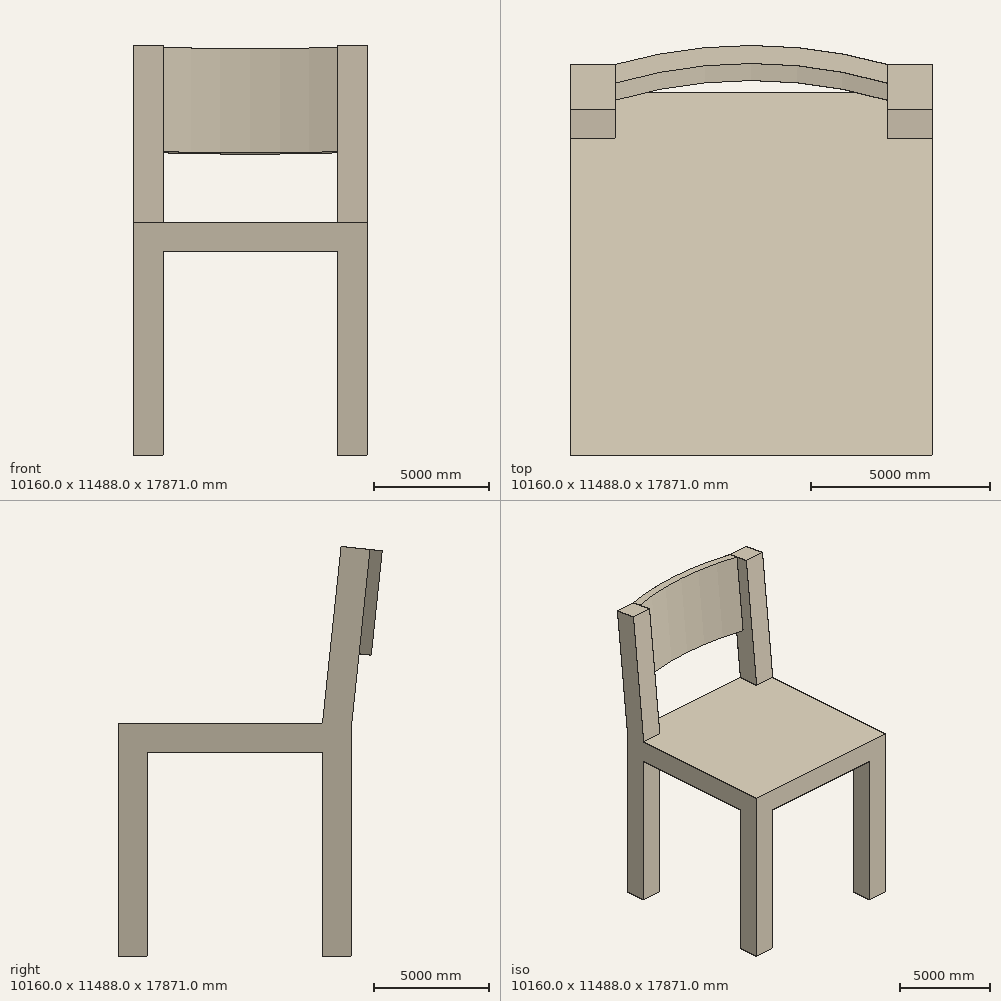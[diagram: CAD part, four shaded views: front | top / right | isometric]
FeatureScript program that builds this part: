
annotation { "Feature Type Name" : "Feature", "Feature Type Description" : "" }
export const myFeature = defineFeature(function(context is Context, id is Id, definition is map)
    precondition{}
    {
        {
            var Q0;
            Q0=qCreatedBy(makeId("Top.planeOp"),FACE);
            var sketch = newSketch(context, id + "F0", { "sketchPlane" : qUnion([Q0])});
            skLineSegment(sketch, "E0.bottom", {"start": v(5080, -5080) * mm, "end": v(-5080, -5080) * mm});
            skLineSegment(sketch, "E0.top", {"start": v(5080, 5080) * mm, "end": v(-5080, 5080) * mm});
            skLineSegment(sketch, "E0.left", {"start": v(5080, -5080) * mm, "end": v(5080, 5080) * mm});
            skLineSegment(sketch, "E0.right", {"start": v(-5080, -5080) * mm, "end": v(-5080, 5080) * mm});
            skPoint(sketch, "E0.middle", {"position": v(0, 0) * mm});
            skSolve(sketch);
        }
        {
            var Q0;
            Q0 = qSketchRegion(id + "F0", true);
            extrude(context, id + "F1", {"entities" : qUnion([Q0]), "depth" : 10160 * mm, "offsetDistance" : 25.4 * mm});
        }
        {
            var Q0;
            Q0=makeQuery(id+"F1.opExtrude","SWEPT_FACE",FACE,{"disambiguationData":[OSD([sQuery(id+"F0.wireOp",EDGE,"E0.bottom")])]});
            var sketch = newSketch(context, id + "F2", { "sketchPlane" : qUnion([Q0])});
            skLineSegment(sketch, "E1.bottom", {"start": v(3810, 8890) * mm, "end": v(-3810, 8890) * mm});
            skLineSegment(sketch, "E1.top", {"start": v(3810, 0) * mm, "end": v(-3810, 0) * mm});
            skLineSegment(sketch, "E1.left", {"start": v(3810, 8890) * mm, "end": v(3810, 0) * mm});
            skLineSegment(sketch, "E1.right", {"start": v(-3810, 8890) * mm, "end": v(-3810, 0) * mm});
            skPoint(sketch, "E1.middle", {"position": v(0, 4445) * mm});
            skSolve(sketch);
        }
        {
            var Q0;
            Q0 = qSketchRegion(id + "F2", true);
            extrude(context, id + "F3", {"entities" : qUnion([Q0]), "operationType" : NewBodyOperationType.REMOVE, "oppositeDirection" : true, "depth" : 12979.4 * mm, "offsetDistance" : 25.4 * mm});
        }
        {
            var Q0;
            Q0=makeQuery(id+"F1.opExtrude","SWEPT_FACE",FACE,{"disambiguationData":[OSD([sQuery(id+"F0.wireOp",EDGE,"E0.right")])]});
            var sketch = newSketch(context, id + "F4", { "sketchPlane" : qUnion([Q0])});
            skLineSegment(sketch, "E2.bottom", {"start": v(3810, 8890) * mm, "end": v(-3810, 8890) * mm});
            skLineSegment(sketch, "E2.top", {"start": v(3810, 0) * mm, "end": v(-3810, 0) * mm});
            skLineSegment(sketch, "E2.left", {"start": v(3810, 8890) * mm, "end": v(3810, 0) * mm});
            skLineSegment(sketch, "E2.right", {"start": v(-3810, 8890) * mm, "end": v(-3810, 0) * mm});
            skPoint(sketch, "E2.middle", {"position": v(0, 4445) * mm});
            skSolve(sketch);
        }
        {
            var Q0;
            Q0 = qSketchRegion(id + "F4", true);
            extrude(context, id + "F5", {"entities" : qUnion([Q0]), "operationType" : NewBodyOperationType.REMOVE, "oppositeDirection" : true, "depth" : 15138.4 * mm, "offsetDistance" : 25.4 * mm});
        }
        {
            var Q0;
            Q0=makeQuery(id+"F1.opExtrude","CAP_FACE",FACE,{"disambiguationData":[OSD([sQuery(id+"F0.wireOp",EDGE,"E0.bottom"),sQuery(id+"F0.wireOp",EDGE,"E0.top"),sQuery(id+"F0.wireOp",EDGE,"E0.left"),sQuery(id+"F0.wireOp",EDGE,"E0.right")])],"isStart":false});
            cPlane(context, id + "F6", {"entities" : qUnion([Q0]), "cplaneType" : CPlaneType.OFFSET, "offset" : 0 * mm, "width" : 152.4 * mm, "height" : 152.4 * mm});
        }
        {
            var Q0;
            Q0=qCreatedBy(id+"F6.planeOp",FACE);
            var sketch = newSketch(context, id + "F7", { "sketchPlane" : qUnion([Q0])});
            skLineSegment(sketch, "E3", {"start": v(8810.43, 5080) * mm, "end": v(-7243.72, 5080) * mm, "construction": true});
            skSolve(sketch);
        }
        {
            var Q0;
            Q0=sQuery(id+"F7.wireOp",EDGE,"E3");
            var Q1;
            Q1=makeQuery(id+"F1.opExtrude","SWEPT_FACE",FACE,{"disambiguationData":[OSD([sQuery(id+"F0.wireOp",EDGE,"E0.top")])]});
            cPlane(context, id + "F8", {"entities" : qUnion([Q0, Q1]), "cplaneType" : CPlaneType.LINE_ANGLE, "offset" : 25.4 * mm, "angle" : 0 * degree, "width" : 152.4 * mm, "height" : 152.4 * mm});
        }
        {
            var Q0;
            Q0=sQuery(id+"F7.wireOp",EDGE,"E3");
            var Q1;
            Q1=qCreatedBy(id+"F8.planeOp",FACE);
            cPlane(context, id + "F9", {"entities" : qUnion([Q0, Q1]), "cplaneType" : CPlaneType.LINE_ANGLE, "offset" : 25.4 * mm, "angle" : 6 * degree, "width" : 152.4 * mm, "height" : 152.4 * mm});
        }
        {
            var Q0;
            Q0=qCreatedBy(id+"F9.planeOp",FACE);
            var sketch = newSketch(context, id + "F10", { "sketchPlane" : qUnion([Q0])});
            skLineSegment(sketch, "E4.bottom", {"start": v(5080, 18255.35) * mm, "end": v(-5080, 18255.35) * mm});
            skLineSegment(sketch, "E4.top", {"start": v(5080, 10635.35) * mm, "end": v(-5080, 10635.35) * mm});
            skLineSegment(sketch, "E4.left", {"start": v(5080, 18255.35) * mm, "end": v(5080, 10635.35) * mm});
            skLineSegment(sketch, "E4.right", {"start": v(-5080, 18255.35) * mm, "end": v(-5080, 10635.35) * mm});
            skSolve(sketch);
        }
        {
            var Q0;
            Q0 = qSketchRegion(id + "F10", true);
            extrude(context, id + "F11", {"entities" : qUnion([Q0]), "oppositeDirection" : true, "depth" : 1270 * mm, "offsetDistance" : 25.4 * mm});
        }
        {
            var Q0;
            Q0=makeQuery(id+"F11.opExtrude","CAP_FACE",FACE,{"disambiguationData":[OSD([sQuery(id+"F10.wireOp",EDGE,"E4.bottom"),sQuery(id+"F10.wireOp",EDGE,"E4.top"),sQuery(id+"F10.wireOp",EDGE,"E4.left"),sQuery(id+"F10.wireOp",EDGE,"E4.right")])],"isStart":false});
            var sketch = newSketch(context, id + "F12", { "sketchPlane" : qUnion([Q0])});
            skLineSegment(sketch, "E5.bottom", {"start": v(-3810, 18255.35) * mm, "end": v(3810, 18255.35) * mm});
            skLineSegment(sketch, "E5.top", {"start": v(-3810, 10635.35) * mm, "end": v(3810, 10635.35) * mm});
            skLineSegment(sketch, "E5.left", {"start": v(-3810, 18255.35) * mm, "end": v(-3810, 10635.35) * mm});
            skLineSegment(sketch, "E5.right", {"start": v(3810, 18255.35) * mm, "end": v(3810, 10635.35) * mm});
            skSolve(sketch);
        }
        {
            var Q0;
            Q0 = qSketchRegion(id + "F12", true);
            extrude(context, id + "F13", {"entities" : qUnion([Q0]), "operationType" : NewBodyOperationType.REMOVE, "oppositeDirection" : true, "depth" : 5130.8 * mm, "offsetDistance" : 25.4 * mm});
        }
        {
            var Q0;
            {var subQ1=sQuery(id+"F10.wireOp",EDGE,"E4.left");var subQ2=sQuery(id+"F10.wireOp",EDGE,"E4.top");Q0=makeQuery(id+"F13.boolean.opBoolean","SPLIT",FACE,{"disambiguationData":[TD([makeQuery(id+"F11.opExtrude","SWEPT_FACE",FACE,{"disambiguationData":[OSD([subQ1])]})])],"derivedFrom":makeQuery(id+"F11.opExtrude","SWEPT_FACE",FACE,{"disambiguationData":[OSD([subQ2])]})});}
            var sketch = newSketch(context, id + "F14", { "sketchPlane" : qUnion([Q0])});
            skSolve(sketch);
        }
        {
            var Q0;
            {var subQ0=sQuery(id+"F10.wireOp",EDGE,"E4.right");var subQ2=sQuery(id+"F10.wireOp",EDGE,"E4.top");Q0=makeQuery(id+"F13.boolean.opBoolean","SPLIT",FACE,{"disambiguationData":[TD([makeQuery(id+"F11.opExtrude","SWEPT_FACE",FACE,{"disambiguationData":[OSD([subQ0])]})])],"derivedFrom":makeQuery(id+"F11.opExtrude","SWEPT_FACE",FACE,{"disambiguationData":[OSD([subQ2])]})});}
            var sketch = newSketch(context, id + "F15", { "sketchPlane" : qUnion([Q0])});
            skSolve(sketch);
        }
        {
            var Q0;
            Q0 = qSketchRegion(id + "F15", true);
            var Q1;
            {var subQ0=sQuery(id+"F10.wireOp",EDGE,"E4.right");var subQ1=sQuery(id+"F10.wireOp",EDGE,"E4.top");Q1=makeQuery(id+"F15.imprint","IMPRINT",FACE,{"disambiguationData":[TD([[makeQuery(id+"F15.imprint","IMPRINT",EDGE,{"derivedFrom":makeQuery(id+"F11.opExtrude","SWEPT_EDGE",EDGE,{"disambiguationData":[OSD([subQ1,subQ0])]})}),-1.0]])]});}
            extrude(context, id + "F16", {"entities" : qUnion([Q0, Q1]), "operationType" : NewBodyOperationType.ADD, "depth" : 170.18 * mm, "offsetDistance" : 25.4 * mm});
        }
        {
            var Q0;
            Q0 = qSketchRegion(id + "F14", true);
            var Q1;
            {var subQ0=sQuery(id+"F10.wireOp",EDGE,"E4.left");var subQ1=sQuery(id+"F10.wireOp",EDGE,"E4.top");Q1=makeQuery(id+"F14.imprint","IMPRINT",FACE,{"disambiguationData":[TD([[makeQuery(id+"F14.imprint","IMPRINT",EDGE,{"derivedFrom":makeQuery(id+"F11.opExtrude","SWEPT_EDGE",EDGE,{"disambiguationData":[OSD([subQ1,subQ0])]})}),1.0]])]});}
            extrude(context, id + "F17", {"entities" : qUnion([Q0, Q1]), "operationType" : NewBodyOperationType.ADD, "depth" : 208.28 * mm, "offsetDistance" : 25.4 * mm});
        }
        {
            var Q0;
            {var subQ1=sQuery(id+"F10.wireOp",EDGE,"E4.left");var subQ3=sQuery(id+"F10.wireOp",EDGE,"E4.bottom");Q0=makeQuery(id+"F13.boolean.opBoolean","SPLIT",FACE,{"disambiguationData":[TD([makeQuery(id+"F11.opExtrude","SWEPT_FACE",FACE,{"disambiguationData":[OSD([subQ1])]})])],"derivedFrom":makeQuery(id+"F11.opExtrude","SWEPT_FACE",FACE,{"disambiguationData":[OSD([subQ3])]})});}
            var sketch = newSketch(context, id + "F18", { "sketchPlane" : qUnion([Q0])});
            skArc(sketch, "E6", {"start": v(3810, 3990.16) * mm, "mid": v(0, 4524.62) * mm, "end": v(-3810, 3990.16) * mm});
            skArc(sketch, "E7.0", {"start": v(3810, 3460.94) * mm, "mid": v(0, 4016.62) * mm, "end": v(-3810, 3460.94) * mm});
            skLineSegment(sketch, "E8", {"start": v(-3810, 3990.16) * mm, "end": v(-3810, 3460.94) * mm});
            skLineSegment(sketch, "E9", {"start": v(3810, 3990.16) * mm, "end": v(3810, 3460.94) * mm});
            skSolve(sketch);
        }
        {
            var Q0;
            Q0 = qSketchRegion(id + "F18", true);
            extrude(context, id + "F19", {"entities" : qUnion([Q0]), "oppositeDirection" : true, "depth" : 4572 * mm, "offsetDistance" : 25.4 * mm});
        }
    });
